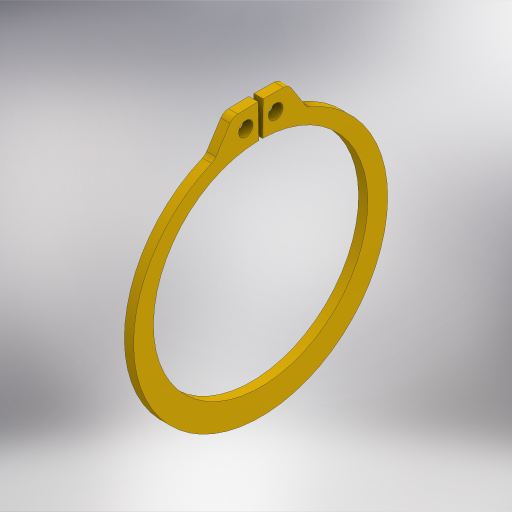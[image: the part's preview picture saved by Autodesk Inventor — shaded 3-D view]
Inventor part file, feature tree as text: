
AUTODESK INVENTOR PART (.ipt)
format: ipt  version: 2024 (Build 280153000, 153)  size: 338,432 bytes
history: native  units: in
note: dims shown in document units (in); Inventor stores cm internally (conversion verified against a paired STEP export)
features: fillet x1
ambient origin geometry x8: Origin, YZ Plane, XZ Plane, XY Plane, X Axis, Y Axis, Z Axis, Center Point
bodies: Solid1 (feature_tree)
feature tree (1):
  fillet  "Fillet1"  [1 undecoded]
note: 1 required parameter value undecoded (feature->parameter linkage not recoverable at this tier; creation-order binding heuristic only, values carry confidence <= 0.55)
